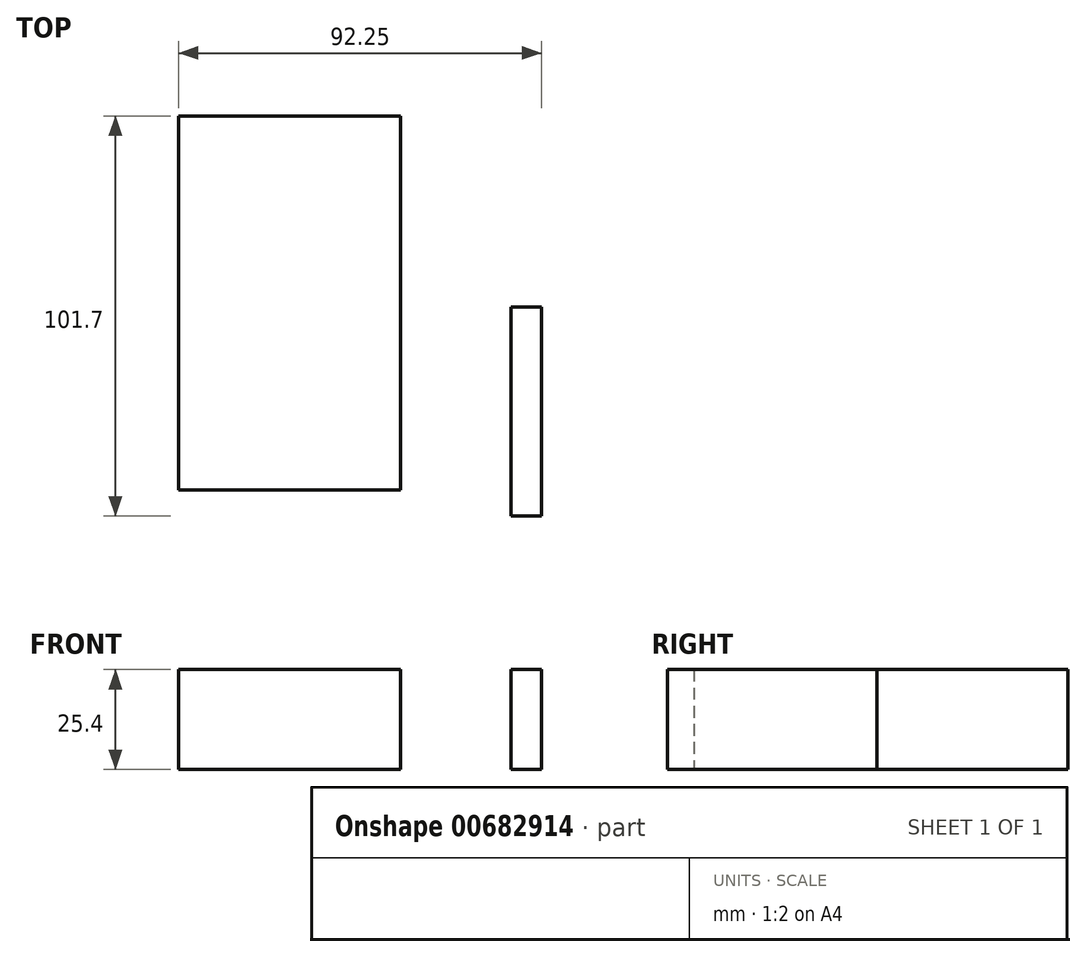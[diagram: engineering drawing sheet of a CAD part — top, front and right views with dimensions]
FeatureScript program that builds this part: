
annotation { "Feature Type Name" : "Feature", "Feature Type Description" : "" }
export const myFeature = defineFeature(function(context is Context, id is Id, definition is map)
    precondition{}
    {
        {
            var Q0;
            Q0=qCreatedBy(makeId("Top.planeOp"),FACE);
            var sketch = newSketch(context, id + "F0", { "sketchPlane" : qUnion([Q0])});
            skLineSegment(sketch, "E0.bottom", {"start": v(0, 48.52) * mm, "end": v(56.42, 48.52) * mm});
            skLineSegment(sketch, "E0.top", {"start": v(0, -46.5) * mm, "end": v(56.42, -46.5) * mm});
            skLineSegment(sketch, "E0.left", {"start": v(0, 48.52) * mm, "end": v(0, -46.5) * mm});
            skLineSegment(sketch, "E0.right", {"start": v(56.42, 48.52) * mm, "end": v(56.42, -46.5) * mm});
            skLineSegment(sketch, "E1.bottom", {"start": v(92.25, 0) * mm, "end": v(84.47, 0) * mm});
            skLineSegment(sketch, "E1.top", {"start": v(92.25, -53.18) * mm, "end": v(84.47, -53.18) * mm});
            skLineSegment(sketch, "E1.left", {"start": v(92.25, 0) * mm, "end": v(92.25, -53.18) * mm});
            skLineSegment(sketch, "E1.right", {"start": v(84.47, 0) * mm, "end": v(84.47, -53.18) * mm});
            skSolve(sketch);
        }
        {
            var Q0;
            Q0 = qSketchRegion(id + "F0", true);
            extrude(context, id + "F1", {"entities" : qUnion([Q0]), "depth" : 25.4 * mm, "offsetDistance" : 25.4 * mm});
        }
    });
